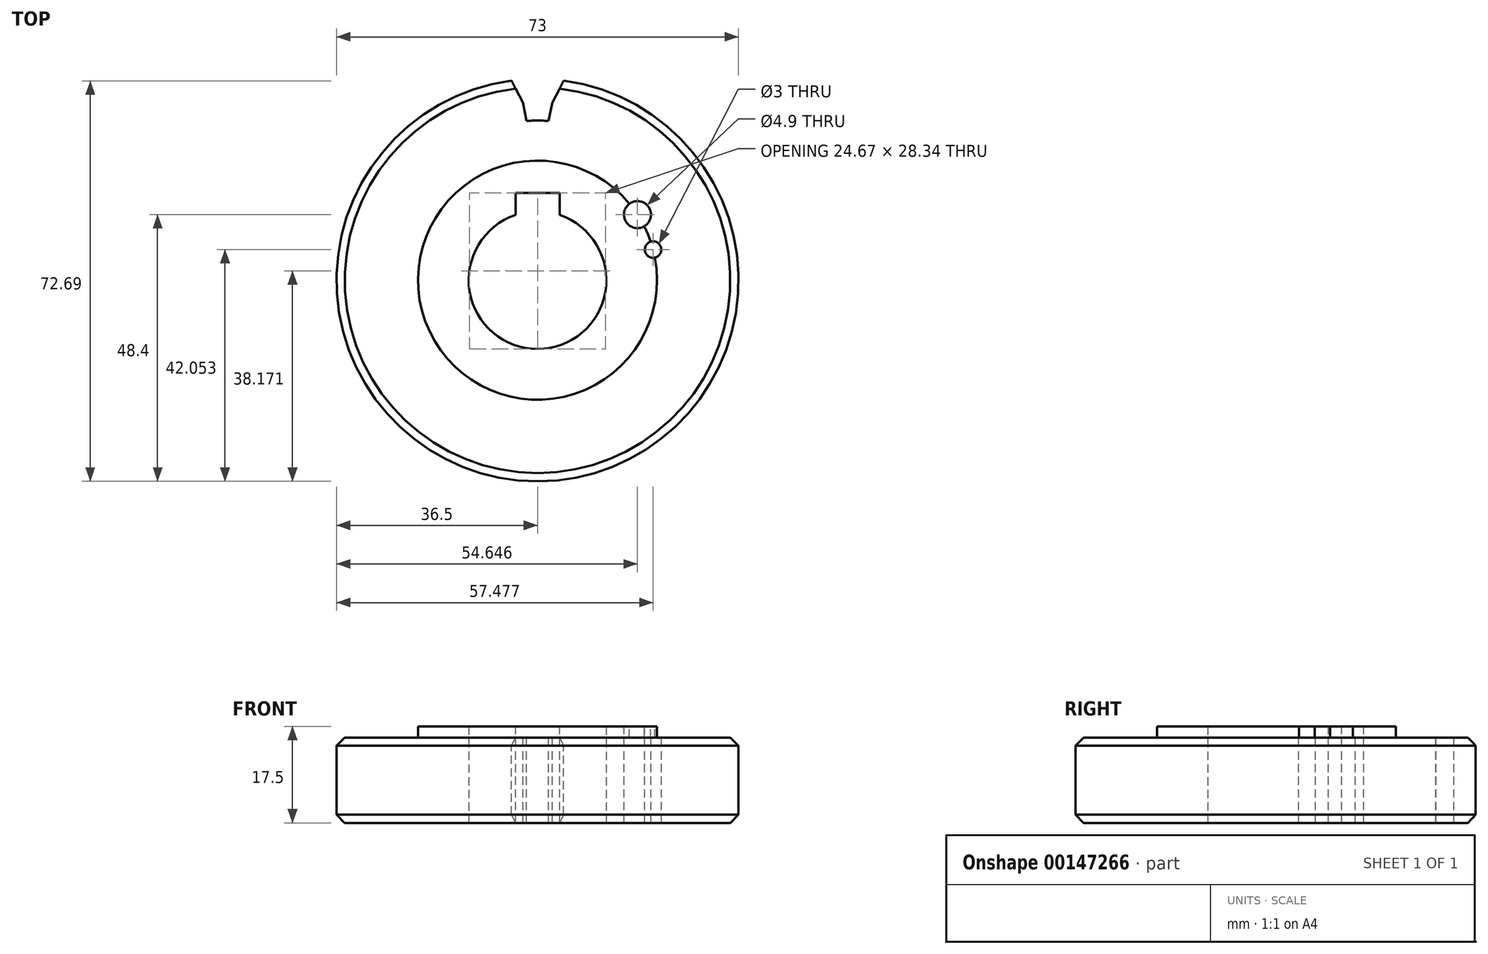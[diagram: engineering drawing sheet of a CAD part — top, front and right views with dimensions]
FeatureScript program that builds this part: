
annotation { "Feature Type Name" : "Feature", "Feature Type Description" : "" }
export const myFeature = defineFeature(function(context is Context, id is Id, definition is map)
    precondition{}
    {
        {
            var Q0;
            Q0=qCreatedBy(makeId("Right.planeOp"),FACE);
            var sketch = newSketch(context, id + "F0", { "sketchPlane" : qUnion([Q0])});
            skLineSegment(sketch, "E0", {"start": v(0, 0) * mm, "end": v(0, 17.5) * mm, "construction": true});
            skLineSegment(sketch, "E1", {"start": v(-36.5, 0) * mm, "end": v(-36.5, 17.5) * mm, "construction": true});
            skLineSegment(sketch, "E2", {"start": v(-21.7, 0) * mm, "end": v(-21.7, 17.5) * mm, "construction": true});
            skLineSegment(sketch, "E3", {"start": v(-12.5, 0) * mm, "end": v(-12.5, 17.5) * mm, "construction": true});
            skLineSegment(sketch, "E4", {"start": v(-12.5, 0) * mm, "end": v(-36.5, 0) * mm});
            skLineSegment(sketch, "E5", {"start": v(-36.5, 0) * mm, "end": v(-36.5, 15.5) * mm});
            skLineSegment(sketch, "E6", {"start": v(-21.7, 15.5) * mm, "end": v(-21.7, 17.5) * mm});
            skLineSegment(sketch, "E7", {"start": v(-36.5, 15.5) * mm, "end": v(-21.7, 15.5) * mm});
            skLineSegment(sketch, "E8", {"start": v(-21.7, 17.5) * mm, "end": v(-12.5, 17.5) * mm});
            skLineSegment(sketch, "E9", {"start": v(-12.5, 17.5) * mm, "end": v(-12.5, 0) * mm});
            skSolve(sketch);
        }
        {
            var Q0;
            Q0=makeQuery(id+"F0.imprint","IMPRINT",FACE,{"disambiguationData":[TD([[makeQuery(id+"F0.imprint","IMPRINT",EDGE,{"derivedFrom":sQuery(id+"F0.wireOp",EDGE,"E4")}),-1.0]])]});
            var Q1;
            Q1=sQuery(id+"F0.wireOp",EDGE,"E0");
            revolve(context, id + "F1", {"entities" : qUnion([Q0]), "axis" : qUnion([Q1]), "revolveType" : RevolveType.FULL});
        }
        {
            var Q0;
            Q0=makeQuery(id+"F1.opRevolve","SWEPT_FACE",FACE,{"disambiguationData":[OSD([sQuery(id+"F0.wireOp",EDGE,"E7")])]});
            var sketch = newSketch(context, id + "F2", { "sketchPlane" : qUnion([Q0])});
            skLineSegment(sketch, "E10", {"start": v(0, 36.5) * mm, "end": v(0, 28.9) * mm, "construction": true});
            skLineSegment(sketch, "E11", {"start": v(-2, 28.9) * mm, "end": v(-2.67, 32.2) * mm});
            skLineSegment(sketch, "E12", {"start": v(0, 36.5) * mm, "end": v(-4.9, 36.5) * mm, "construction": true});
            skLineSegment(sketch, "E13", {"start": v(-2.67, 32.2) * mm, "end": v(-4.9, 36.5) * mm});
            skLineSegment(sketch, "E14", {"start": v(-4.9, 36.5) * mm, "end": v(0, 36.5) * mm});
            skLineSegment(sketch, "E15.MirrorCS", {"start": v(2, 28.9) * mm, "end": v(2.67, 32.2) * mm});
            skLineSegment(sketch, "E16.MirrorCS", {"start": v(2.67, 32.2) * mm, "end": v(4.9, 36.5) * mm});
            skLineSegment(sketch, "E17.MirrorCS", {"start": v(0, 36.5) * mm, "end": v(4.9, 36.5) * mm, "construction": true});
            skLineSegment(sketch, "E18", {"start": v(-4.9, 36.5) * mm, "end": v(4.9, 36.5) * mm});
            skLineSegment(sketch, "E19.1.0", {"start": v(-12.98, 29.59) * mm, "end": v(-16.49, 32.93) * mm});
            skLineSegment(sketch, "E19.1.1", {"start": v(-11.28, 26.68) * mm, "end": v(-12.98, 29.59) * mm});
            skLineSegment(sketch, "E19.1.2", {"start": v(-9.38, 27.33) * mm, "end": v(-11.28, 26.68) * mm});
            skLineSegment(sketch, "E19.1.3", {"start": v(-9.38, 27.33) * mm, "end": v(-7.5, 27.98) * mm});
            skLineSegment(sketch, "E19.1.4", {"start": v(-7.5, 27.98) * mm, "end": v(-7.93, 31.32) * mm});
            skLineSegment(sketch, "E19.1.5", {"start": v(-7.93, 31.32) * mm, "end": v(-7.22, 36.11) * mm});
            skLineSegment(sketch, "E19.1.6", {"start": v(-11.85, 34.52) * mm, "end": v(-7.22, 36.11) * mm, "construction": true});
            skLineSegment(sketch, "E19.1.7", {"start": v(-11.85, 34.52) * mm, "end": v(-16.49, 32.93) * mm, "construction": true});
            skLineSegment(sketch, "E19.2.0", {"start": v(-21.88, 23.77) * mm, "end": v(-26.29, 25.8) * mm});
            skLineSegment(sketch, "E19.2.1", {"start": v(-19.33, 21.58) * mm, "end": v(-21.88, 23.77) * mm});
            skLineSegment(sketch, "E19.2.2", {"start": v(-17.75, 22.8) * mm, "end": v(-19.33, 21.58) * mm});
            skLineSegment(sketch, "E19.2.3", {"start": v(-17.75, 22.8) * mm, "end": v(-16.17, 24.03) * mm});
            skLineSegment(sketch, "E19.2.4", {"start": v(-16.17, 24.03) * mm, "end": v(-17.67, 27.05) * mm});
            skLineSegment(sketch, "E19.2.5", {"start": v(-17.67, 27.05) * mm, "end": v(-18.55, 31.81) * mm});
            skLineSegment(sketch, "E19.2.6", {"start": v(-22.42, 28.8) * mm, "end": v(-18.55, 31.81) * mm, "construction": true});
            skLineSegment(sketch, "E19.2.7", {"start": v(-22.42, 28.8) * mm, "end": v(-26.29, 25.8) * mm, "construction": true});
            skLineSegment(sketch, "E19.3.0", {"start": v(-28.42, 15.38) * mm, "end": v(-33.24, 15.86) * mm});
            skLineSegment(sketch, "E19.3.1", {"start": v(-25.29, 14.13) * mm, "end": v(-28.42, 15.38) * mm});
            skLineSegment(sketch, "E19.3.2", {"start": v(-24.2, 15.8) * mm, "end": v(-25.29, 14.13) * mm});
            skLineSegment(sketch, "E19.3.3", {"start": v(-24.2, 15.8) * mm, "end": v(-23.1, 17.48) * mm});
            skLineSegment(sketch, "E19.3.4", {"start": v(-23.1, 17.48) * mm, "end": v(-25.5, 19.85) * mm});
            skLineSegment(sketch, "E19.3.5", {"start": v(-25.5, 19.85) * mm, "end": v(-27.88, 24.07) * mm});
            skLineSegment(sketch, "E19.3.6", {"start": v(-30.56, 19.96) * mm, "end": v(-27.88, 24.07) * mm, "construction": true});
            skLineSegment(sketch, "E19.3.7", {"start": v(-30.56, 19.96) * mm, "end": v(-33.24, 15.86) * mm, "construction": true});
            skLineSegment(sketch, "E19.4.0", {"start": v(-31.87, 5.32) * mm, "end": v(-36.59, 4.21) * mm});
            skLineSegment(sketch, "E19.4.1", {"start": v(-28.5, 5.16) * mm, "end": v(-31.87, 5.32) * mm});
            skLineSegment(sketch, "E19.4.2", {"start": v(-28.02, 7.1) * mm, "end": v(-28.5, 5.16) * mm});
            skLineSegment(sketch, "E19.4.3", {"start": v(-28.02, 7.1) * mm, "end": v(-27.52, 9.03) * mm});
            skLineSegment(sketch, "E19.4.4", {"start": v(-27.52, 9.03) * mm, "end": v(-30.56, 10.5) * mm});
            skLineSegment(sketch, "E19.4.5", {"start": v(-30.56, 10.5) * mm, "end": v(-34.18, 13.71) * mm});
            skLineSegment(sketch, "E19.4.6", {"start": v(-35.38, 8.96) * mm, "end": v(-34.18, 13.71) * mm, "construction": true});
            skLineSegment(sketch, "E19.4.7", {"start": v(-35.38, 8.96) * mm, "end": v(-36.59, 4.21) * mm, "construction": true});
            skLineSegment(sketch, "E19.5.0", {"start": v(-31.87, -5.32) * mm, "end": v(-35.97, -7.9) * mm});
            skLineSegment(sketch, "E19.5.1", {"start": v(-28.64, -4.38) * mm, "end": v(-31.87, -5.32) * mm});
            skLineSegment(sketch, "E19.5.2", {"start": v(-28.8, -2.39) * mm, "end": v(-28.64, -4.38) * mm});
            skLineSegment(sketch, "E19.5.3", {"start": v(-28.8, -2.39) * mm, "end": v(-28.97, -0.4) * mm});
            skLineSegment(sketch, "E19.5.4", {"start": v(-28.97, -0.4) * mm, "end": v(-32.31, 0) * mm});
            skLineSegment(sketch, "E19.5.5", {"start": v(-32.31, 0) * mm, "end": v(-36.78, 1.87) * mm});
            skLineSegment(sketch, "E19.5.6", {"start": v(-36.38, -3.01) * mm, "end": v(-36.78, 1.87) * mm, "construction": true});
            skLineSegment(sketch, "E19.5.7", {"start": v(-36.38, -3.01) * mm, "end": v(-35.97, -7.9) * mm, "construction": true});
            skLineSegment(sketch, "E19.6.0", {"start": v(-28.42, -15.38) * mm, "end": v(-31.46, -19.15) * mm});
            skLineSegment(sketch, "E19.6.1", {"start": v(-25.66, -13.44) * mm, "end": v(-28.42, -15.38) * mm});
            skLineSegment(sketch, "E19.6.2", {"start": v(-26.47, -11.6) * mm, "end": v(-25.66, -13.44) * mm});
            skLineSegment(sketch, "E19.6.3", {"start": v(-26.47, -11.6) * mm, "end": v(-27.27, -9.78) * mm});
            skLineSegment(sketch, "E19.6.4", {"start": v(-27.27, -9.78) * mm, "end": v(-30.56, -10.5) * mm});
            skLineSegment(sketch, "E19.6.5", {"start": v(-30.56, -10.5) * mm, "end": v(-35.4, -10.17) * mm});
            skLineSegment(sketch, "E19.6.6", {"start": v(-33.43, -14.66) * mm, "end": v(-35.4, -10.17) * mm, "construction": true});
            skLineSegment(sketch, "E19.6.7", {"start": v(-33.43, -14.66) * mm, "end": v(-31.46, -19.15) * mm, "construction": true});
            skLineSegment(sketch, "E19.7.0", {"start": v(-21.88, -23.77) * mm, "end": v(-23.54, -28.33) * mm});
            skLineSegment(sketch, "E19.7.1", {"start": v(-19.9, -21.04) * mm, "end": v(-21.88, -23.77) * mm});
            skLineSegment(sketch, "E19.7.2", {"start": v(-21.26, -19.57) * mm, "end": v(-19.9, -21.04) * mm});
            skLineSegment(sketch, "E19.7.3", {"start": v(-21.26, -19.57) * mm, "end": v(-22.62, -18.1) * mm});
            skLineSegment(sketch, "E19.7.4", {"start": v(-22.62, -18.1) * mm, "end": v(-25.5, -19.85) * mm});
            skLineSegment(sketch, "E19.7.5", {"start": v(-25.5, -19.85) * mm, "end": v(-30.17, -21.12) * mm});
            skLineSegment(sketch, "E19.7.6", {"start": v(-26.85, -24.72) * mm, "end": v(-30.17, -21.12) * mm, "construction": true});
            skLineSegment(sketch, "E19.7.7", {"start": v(-26.85, -24.72) * mm, "end": v(-23.54, -28.33) * mm, "construction": true});
            skLineSegment(sketch, "E19.8.0", {"start": v(-12.98, -29.59) * mm, "end": v(-13.06, -34.43) * mm});
            skLineSegment(sketch, "E19.8.1", {"start": v(-12, -26.37) * mm, "end": v(-12.98, -29.59) * mm});
            skLineSegment(sketch, "E19.8.2", {"start": v(-13.75, -25.42) * mm, "end": v(-12, -26.37) * mm});
            skLineSegment(sketch, "E19.8.3", {"start": v(-13.75, -25.42) * mm, "end": v(-15.51, -24.46) * mm});
            skLineSegment(sketch, "E19.8.4", {"start": v(-15.51, -24.46) * mm, "end": v(-17.67, -27.05) * mm});
            skLineSegment(sketch, "E19.8.5", {"start": v(-17.67, -27.05) * mm, "end": v(-21.68, -29.77) * mm});
            skLineSegment(sketch, "E19.8.6", {"start": v(-17.37, -32.1) * mm, "end": v(-21.68, -29.77) * mm, "construction": true});
            skLineSegment(sketch, "E19.8.7", {"start": v(-17.37, -32.1) * mm, "end": v(-13.06, -34.43) * mm, "construction": true});
            skLineSegment(sketch, "E19.9.0", {"start": v(-2.67, -32.2) * mm, "end": v(-1.17, -36.8) * mm});
            skLineSegment(sketch, "E19.9.1", {"start": v(-2.78, -28.84) * mm, "end": v(-2.67, -32.2) * mm});
            skLineSegment(sketch, "E19.9.2", {"start": v(-4.76, -28.5) * mm, "end": v(-2.78, -28.84) * mm});
            skLineSegment(sketch, "E19.9.3", {"start": v(-4.76, -28.5) * mm, "end": v(-6.73, -28.18) * mm});
            skLineSegment(sketch, "E19.9.4", {"start": v(-6.73, -28.18) * mm, "end": v(-7.93, -31.32) * mm});
            skLineSegment(sketch, "E19.9.5", {"start": v(-7.93, -31.32) * mm, "end": v(-10.84, -35.2) * mm});
            skLineSegment(sketch, "E19.9.6", {"start": v(-6, -36) * mm, "end": v(-10.84, -35.2) * mm, "construction": true});
            skLineSegment(sketch, "E19.9.7", {"start": v(-6, -36) * mm, "end": v(-1.17, -36.8) * mm, "construction": true});
            skLineSegment(sketch, "E19.10.0", {"start": v(7.93, -31.32) * mm, "end": v(10.84, -35.2) * mm});
            skLineSegment(sketch, "E19.10.1", {"start": v(6.73, -28.18) * mm, "end": v(7.93, -31.32) * mm});
            skLineSegment(sketch, "E19.10.2", {"start": v(4.76, -28.5) * mm, "end": v(6.73, -28.18) * mm});
            skLineSegment(sketch, "E19.10.3", {"start": v(4.76, -28.5) * mm, "end": v(2.78, -28.84) * mm});
            skLineSegment(sketch, "E19.10.4", {"start": v(2.78, -28.84) * mm, "end": v(2.67, -32.2) * mm});
            skLineSegment(sketch, "E19.10.5", {"start": v(2.67, -32.2) * mm, "end": v(1.17, -36.8) * mm});
            skLineSegment(sketch, "E19.10.6", {"start": v(6, -36) * mm, "end": v(1.17, -36.8) * mm, "construction": true});
            skLineSegment(sketch, "E19.10.7", {"start": v(6, -36) * mm, "end": v(10.84, -35.2) * mm, "construction": true});
            skLineSegment(sketch, "E19.11.0", {"start": v(17.67, -27.05) * mm, "end": v(21.68, -29.77) * mm});
            skLineSegment(sketch, "E19.11.1", {"start": v(15.51, -24.46) * mm, "end": v(17.67, -27.05) * mm});
            skLineSegment(sketch, "E19.11.2", {"start": v(13.75, -25.42) * mm, "end": v(15.51, -24.46) * mm});
            skLineSegment(sketch, "E19.11.3", {"start": v(13.75, -25.42) * mm, "end": v(12, -26.37) * mm});
            skLineSegment(sketch, "E19.11.4", {"start": v(12, -26.37) * mm, "end": v(12.98, -29.59) * mm});
            skLineSegment(sketch, "E19.11.5", {"start": v(12.98, -29.59) * mm, "end": v(13.06, -34.43) * mm});
            skLineSegment(sketch, "E19.11.6", {"start": v(17.37, -32.1) * mm, "end": v(13.06, -34.43) * mm, "construction": true});
            skLineSegment(sketch, "E19.11.7", {"start": v(17.37, -32.1) * mm, "end": v(21.68, -29.77) * mm, "construction": true});
            skLineSegment(sketch, "E19.12.0", {"start": v(25.5, -19.85) * mm, "end": v(30.17, -21.12) * mm});
            skLineSegment(sketch, "E19.12.1", {"start": v(22.62, -18.1) * mm, "end": v(25.5, -19.85) * mm});
            skLineSegment(sketch, "E19.12.2", {"start": v(21.26, -19.57) * mm, "end": v(22.62, -18.1) * mm});
            skLineSegment(sketch, "E19.12.3", {"start": v(21.26, -19.57) * mm, "end": v(19.9, -21.04) * mm});
            skLineSegment(sketch, "E19.12.4", {"start": v(19.9, -21.04) * mm, "end": v(21.88, -23.77) * mm});
            skLineSegment(sketch, "E19.12.5", {"start": v(21.88, -23.77) * mm, "end": v(23.54, -28.33) * mm});
            skLineSegment(sketch, "E19.12.6", {"start": v(26.85, -24.72) * mm, "end": v(23.54, -28.33) * mm, "construction": true});
            skLineSegment(sketch, "E19.12.7", {"start": v(26.85, -24.72) * mm, "end": v(30.17, -21.12) * mm, "construction": true});
            skLineSegment(sketch, "E19.13.0", {"start": v(30.56, -10.5) * mm, "end": v(35.4, -10.17) * mm});
            skLineSegment(sketch, "E19.13.1", {"start": v(27.27, -9.78) * mm, "end": v(30.56, -10.5) * mm});
            skLineSegment(sketch, "E19.13.2", {"start": v(26.47, -11.6) * mm, "end": v(27.27, -9.78) * mm});
            skLineSegment(sketch, "E19.13.3", {"start": v(26.47, -11.6) * mm, "end": v(25.66, -13.44) * mm});
            skLineSegment(sketch, "E19.13.4", {"start": v(25.66, -13.44) * mm, "end": v(28.42, -15.38) * mm});
            skLineSegment(sketch, "E19.13.5", {"start": v(28.42, -15.38) * mm, "end": v(31.46, -19.15) * mm});
            skLineSegment(sketch, "E19.13.6", {"start": v(33.43, -14.66) * mm, "end": v(31.46, -19.15) * mm, "construction": true});
            skLineSegment(sketch, "E19.13.7", {"start": v(33.43, -14.66) * mm, "end": v(35.4, -10.17) * mm, "construction": true});
            skLineSegment(sketch, "E19.14.0", {"start": v(32.31, 0) * mm, "end": v(36.78, 1.87) * mm});
            skLineSegment(sketch, "E19.14.1", {"start": v(28.97, -0.4) * mm, "end": v(32.31, 0) * mm});
            skLineSegment(sketch, "E19.14.2", {"start": v(28.8, -2.39) * mm, "end": v(28.97, -0.4) * mm});
            skLineSegment(sketch, "E19.14.3", {"start": v(28.8, -2.39) * mm, "end": v(28.64, -4.38) * mm});
            skLineSegment(sketch, "E19.14.4", {"start": v(28.64, -4.38) * mm, "end": v(31.87, -5.32) * mm});
            skLineSegment(sketch, "E19.14.5", {"start": v(31.87, -5.32) * mm, "end": v(35.97, -7.9) * mm});
            skLineSegment(sketch, "E19.14.6", {"start": v(36.38, -3.01) * mm, "end": v(35.97, -7.9) * mm, "construction": true});
            skLineSegment(sketch, "E19.14.7", {"start": v(36.38, -3.01) * mm, "end": v(36.78, 1.87) * mm, "construction": true});
            skLineSegment(sketch, "E19.15.0", {"start": v(30.56, 10.5) * mm, "end": v(34.18, 13.71) * mm});
            skLineSegment(sketch, "E19.15.1", {"start": v(27.52, 9.03) * mm, "end": v(30.56, 10.5) * mm});
            skLineSegment(sketch, "E19.15.2", {"start": v(28.02, 7.1) * mm, "end": v(27.52, 9.03) * mm});
            skLineSegment(sketch, "E19.15.3", {"start": v(28.02, 7.1) * mm, "end": v(28.5, 5.16) * mm});
            skLineSegment(sketch, "E19.15.4", {"start": v(28.5, 5.16) * mm, "end": v(31.87, 5.32) * mm});
            skLineSegment(sketch, "E19.15.5", {"start": v(31.87, 5.32) * mm, "end": v(36.59, 4.21) * mm});
            skLineSegment(sketch, "E19.15.6", {"start": v(35.38, 8.96) * mm, "end": v(36.59, 4.21) * mm, "construction": true});
            skLineSegment(sketch, "E19.15.7", {"start": v(35.38, 8.96) * mm, "end": v(34.18, 13.71) * mm, "construction": true});
            skLineSegment(sketch, "E19.16.0", {"start": v(25.5, 19.85) * mm, "end": v(27.88, 24.07) * mm});
            skLineSegment(sketch, "E19.16.1", {"start": v(23.1, 17.48) * mm, "end": v(25.5, 19.85) * mm});
            skLineSegment(sketch, "E19.16.2", {"start": v(24.2, 15.8) * mm, "end": v(23.1, 17.48) * mm});
            skLineSegment(sketch, "E19.16.3", {"start": v(24.2, 15.8) * mm, "end": v(25.29, 14.13) * mm});
            skLineSegment(sketch, "E19.16.4", {"start": v(25.29, 14.13) * mm, "end": v(28.42, 15.38) * mm});
            skLineSegment(sketch, "E19.16.5", {"start": v(28.42, 15.38) * mm, "end": v(33.24, 15.86) * mm});
            skLineSegment(sketch, "E19.16.6", {"start": v(30.56, 19.96) * mm, "end": v(33.24, 15.86) * mm, "construction": true});
            skLineSegment(sketch, "E19.16.7", {"start": v(30.56, 19.96) * mm, "end": v(27.88, 24.07) * mm, "construction": true});
            skLineSegment(sketch, "E19.17.0", {"start": v(17.67, 27.05) * mm, "end": v(18.55, 31.81) * mm});
            skLineSegment(sketch, "E19.17.1", {"start": v(16.17, 24.03) * mm, "end": v(17.67, 27.05) * mm});
            skLineSegment(sketch, "E19.17.2", {"start": v(17.75, 22.8) * mm, "end": v(16.17, 24.03) * mm});
            skLineSegment(sketch, "E19.17.3", {"start": v(17.75, 22.8) * mm, "end": v(19.33, 21.58) * mm});
            skLineSegment(sketch, "E19.17.4", {"start": v(19.33, 21.58) * mm, "end": v(21.88, 23.77) * mm});
            skLineSegment(sketch, "E19.17.5", {"start": v(21.88, 23.77) * mm, "end": v(26.29, 25.8) * mm});
            skLineSegment(sketch, "E19.17.6", {"start": v(22.42, 28.8) * mm, "end": v(26.29, 25.8) * mm, "construction": true});
            skLineSegment(sketch, "E19.17.7", {"start": v(22.42, 28.8) * mm, "end": v(18.55, 31.81) * mm, "construction": true});
            skLineSegment(sketch, "E19.18.0", {"start": v(7.93, 31.32) * mm, "end": v(7.22, 36.11) * mm});
            skLineSegment(sketch, "E19.18.1", {"start": v(7.5, 27.98) * mm, "end": v(7.93, 31.32) * mm});
            skLineSegment(sketch, "E19.18.2", {"start": v(9.38, 27.33) * mm, "end": v(7.5, 27.98) * mm});
            skLineSegment(sketch, "E19.18.3", {"start": v(9.38, 27.33) * mm, "end": v(11.28, 26.68) * mm});
            skLineSegment(sketch, "E19.18.4", {"start": v(11.28, 26.68) * mm, "end": v(12.98, 29.59) * mm});
            skLineSegment(sketch, "E19.18.5", {"start": v(12.98, 29.59) * mm, "end": v(16.49, 32.93) * mm});
            skLineSegment(sketch, "E19.18.6", {"start": v(11.85, 34.52) * mm, "end": v(16.49, 32.93) * mm, "construction": true});
            skLineSegment(sketch, "E19.18.7", {"start": v(11.85, 34.52) * mm, "end": v(7.22, 36.11) * mm, "construction": true});
            skPoint(sketch, "E19.center", {"position": v(0, 0) * mm});
            skPoint(sketch, "E20.MirrorCS.end.orphan", {"position": v(2, 28.9) * mm});
            skPoint(sketch, "E20.MirrorCS.start.orphan", {"position": v(0, 28.9) * mm});
            skArc(sketch, "E21", {"start": v(2, 28.9) * mm, "mid": v(0, 28.97) * mm, "end": v(-2, 28.9) * mm});
            skArc(sketch, "E22.trimOffspring", {"start": v(-7.5, 27.98) * mm, "mid": v(0, -28.97) * mm, "end": v(7.5, 27.98) * mm});
            skSolve(sketch);
        }
        {
            var Q0;
            {var subQ7=sQuery(id+"F2.wireOp",EDGE,"E11");Q0=makeQuery(id+"F2.imprint","IMPRINT",FACE,{"disambiguationData":[TD([[makeQuery(id+"F2.imprint","IMPRINT",EDGE,{"derivedFrom":subQ7}),-1.0]])]});}
            extrude(context, id + "F3", {"entities" : qUnion([Q0]), "operationType" : NewBodyOperationType.REMOVE, "endBound" : BoundingType.THROUGH_ALL, "oppositeDirection" : true, "depth" : 25 * mm});
        }
        {
            var Q0;
            Q0=qCreatedBy(makeId("Right.planeOp"),FACE);
            var sketch = newSketch(context, id + "F4", { "sketchPlane" : qUnion([Q0])});
            skLineSegment(sketch, "E23", {"start": v(0, -17.18) * mm, "end": v(0, 39.42) * mm, "construction": true});
            skSolve(sketch);
        }
        {
            var Q0;
            Q0=makeQuery(id+"F1.opRevolve","SWEPT_EDGE",EDGE,{"disambiguationData":[OSD([sQuery(id+"F0.wireOp",EDGE,"E4"),sQuery(id+"F0.wireOp",EDGE,"E5")])]});
            var Q1;
            Q1=makeQuery(id+"F1.opRevolve","SWEPT_EDGE",EDGE,{"disambiguationData":[OSD([sQuery(id+"F0.wireOp",EDGE,"E5"),sQuery(id+"F0.wireOp",EDGE,"E7")])]});
            chamfer(context, id + "F5", {"entities" : qUnion([Q0, Q1]), "width" : 1.5 * mm, "tangentPropagation" : true});
        }
        {
            var Q0;
            Q0=makeQuery(id+"F1.opRevolve","SWEPT_FACE",FACE,{"disambiguationData":[OSD([sQuery(id+"F0.wireOp",EDGE,"E8")])]});
            var sketch = newSketch(context, id + "F6", { "sketchPlane" : qUnion([Q0])});
            skLineSegment(sketch, "E24", {"start": v(0, 12.5) * mm, "end": v(0, 16.5) * mm, "construction": true});
            skLineSegment(sketch, "E25", {"start": v(0, 12.5) * mm, "end": v(-4, 12.5) * mm, "construction": true});
            skLineSegment(sketch, "E26", {"start": v(-4, 11.84) * mm, "end": v(-4, 15.84) * mm});
            skLineSegment(sketch, "E27", {"start": v(-4, 15.84) * mm, "end": v(0, 15.84) * mm});
            skLineSegment(sketch, "E28.MirrorCS", {"start": v(4, 15.84) * mm, "end": v(0, 15.84) * mm});
            skLineSegment(sketch, "E29.MirrorCS", {"start": v(4, 11.84) * mm, "end": v(4, 15.84) * mm});
            skLineSegment(sketch, "E30", {"start": v(4, 11.84) * mm, "end": v(-4, 11.84) * mm});
            skSolve(sketch);
        }
        {
            var Q0;
            Q0 = qSketchRegion(id + "F6", true);
            extrude(context, id + "F7", {"entities" : qUnion([Q0]), "operationType" : NewBodyOperationType.REMOVE, "endBound" : BoundingType.THROUGH_ALL, "oppositeDirection" : true, "depth" : 25 * mm});
        }
        {
            var Q0;
            Q0=makeQuery(id+"F1.opRevolve","SWEPT_FACE",FACE,{"disambiguationData":[OSD([sQuery(id+"F0.wireOp",EDGE,"E8")])]});
            var sketch = newSketch(context, id + "F8", { "sketchPlane" : qUnion([Q0])});
            skCircle(sketch, "E31", {"center": v(18.15, 11.9) * mm, "radius": 2.45 * mm});
            skCircle(sketch, "E32", {"center": v(20.98, 5.55) * mm, "radius": 1.5 * mm});
            skSolve(sketch);
        }
        {
            var Q0;
            Q0 = qSketchRegion(id + "F8", true);
            extrude(context, id + "F9", {"entities" : qUnion([Q0]), "operationType" : NewBodyOperationType.REMOVE, "endBound" : BoundingType.THROUGH_ALL, "oppositeDirection" : true, "depth" : 25 * mm});
        }
    });
